# Revit family: Viking Roofspec Drain 04 M01
name_source: partatom
category: Pipe Fittings
units: mm (PartAtom-declared; Revit-internal decimal feet)

## family parameters
Cut with Voids When Loaded = No
Host = Face
Part Type = Cap
Round Connector Dimension = Use Diameter
Shared = No

## types (1)
- Drains - Deck Drain - 100mm
    Component = SDM049-050 : Deck Drain
    Cut Diameter = 185 mm  [stored 0.606955 ft]
    Default Elevation = 0 mm  [stored 0 ft]
    Flow Out = 5.1 L/s
    Grate Material = Viking Roofspec - Stainless Steel
    Manufacturer = Viking Roofspec
    Material = Viking Roofspec - Plastic White
    Model = SDM050
    Overall Cut Diameter = 230 mm  [stored 0.754593 ft]
    Pipe Diameter = 100 mm  [stored 0.328084 ft]
    Type Comments = Viking Roofspec 100mmØ clamped deck drain SDM050 with 304 S/S flat grate, installed as per manufacturers instructions.
    URL = www.vikingroofspec.co.nz

note: [stored X ft] marks values corroborated as IEEE doubles in the binary element streams (Revit-internal decimal feet)

## geometry (parser evidence)
native form markers: Sweep x18
no freeform markers — native parametric forms only
